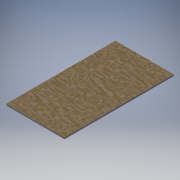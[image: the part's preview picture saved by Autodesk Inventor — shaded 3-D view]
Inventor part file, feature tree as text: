
AUTODESK INVENTOR PART (.ipt)
format: ipt  version: 2018.2 (Build 222227000, 227)  size: 110,080 bytes
history: native  units: in
note: dims shown in document units (in); Inventor stores cm internally (conversion verified against a paired STEP export)
features: extrude x1, sketch x1
ambient origin geometry x8: Origin, YZ Plane, XZ Plane, XY Plane, X Axis, Y Axis, Z Axis, Center Point
bodies: Solid1 (feature_tree)
feature tree (2):
  extrude  "Extrusion1"  Depth=0.75in
  sketch  "Sketch1"  dims[d0=28.226in d1=0.75in d2=52.898in d3=0.0in]
